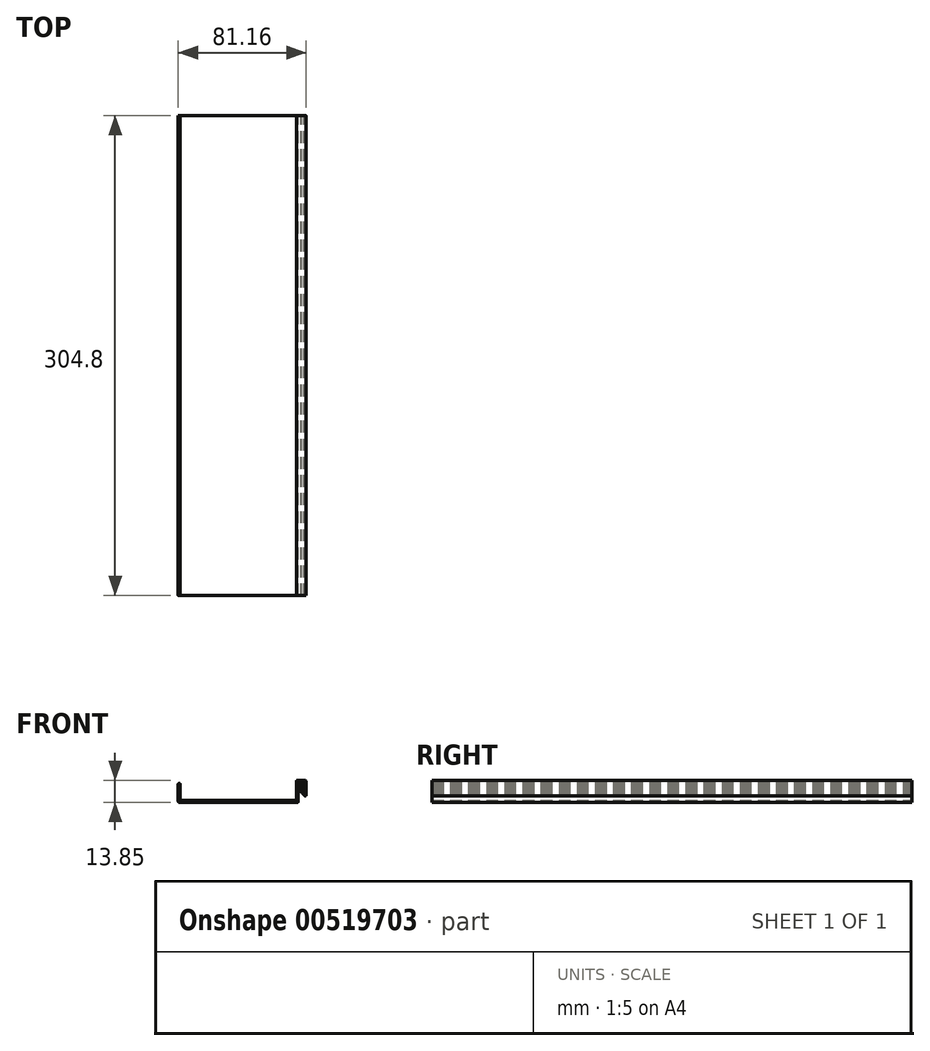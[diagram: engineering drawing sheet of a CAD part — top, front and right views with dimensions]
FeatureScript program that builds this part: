
annotation { "Feature Type Name" : "Feature", "Feature Type Description" : "" }
export const myFeature = defineFeature(function(context is Context, id is Id, definition is map)
    precondition{}
    {
        {
            var Q0;
            Q0=qCreatedBy(makeId("Front.planeOp"),FACE);
            var sketch = newSketch(context, id + "F0", { "sketchPlane" : qUnion([Q0])});
            skArc(sketch, "E0", {"start": v(-471.73, -378.6) * mm, "mid": v(-471.73, -378.44) * mm, "end": v(-471.88, -378.35) * mm});
            skArc(sketch, "E1", {"start": v(-475.36, -380.7) * mm, "mid": v(-473.26, -380.15) * mm, "end": v(-471.73, -378.6) * mm});
            skArc(sketch, "E2", {"start": v(-475.5, -380.45) * mm, "mid": v(-475.5, -380.61) * mm, "end": v(-475.36, -380.7) * mm});
            skArc(sketch, "E3", {"start": v(-471.88, -378.35) * mm, "mid": v(-473.98, -378.9) * mm, "end": v(-475.5, -380.45) * mm});
            skArc(sketch, "E4", {"start": v(-471.73, -372.86) * mm, "mid": v(-471.73, -372.7) * mm, "end": v(-471.88, -372.6) * mm});
            skArc(sketch, "E5", {"start": v(-475.36, -374.95) * mm, "mid": v(-473.26, -374.4) * mm, "end": v(-471.73, -372.86) * mm});
            skArc(sketch, "E6", {"start": v(-475.5, -374.7) * mm, "mid": v(-475.5, -374.87) * mm, "end": v(-475.36, -374.95) * mm});
            skArc(sketch, "E7", {"start": v(-471.88, -372.6) * mm, "mid": v(-473.98, -373.15) * mm, "end": v(-475.5, -374.7) * mm});
            skArc(sketch, "E8", {"start": v(-467.73, -383.43) * mm, "mid": v(-467.59, -383.35) * mm, "end": v(-467.59, -383.18) * mm});
            skArc(sketch, "E9", {"start": v(-471.36, -381.34) * mm, "mid": v(-469.83, -382.89) * mm, "end": v(-467.73, -383.43) * mm});
            skArc(sketch, "E10", {"start": v(-471.21, -381.09) * mm, "mid": v(-471.36, -381.17) * mm, "end": v(-471.36, -381.34) * mm});
            skArc(sketch, "E11", {"start": v(-467.59, -383.18) * mm, "mid": v(-469.1, -381.63) * mm, "end": v(-471.21, -381.09) * mm});
            skArc(sketch, "E12", {"start": v(-467.73, -377.9) * mm, "mid": v(-467.59, -377.82) * mm, "end": v(-467.59, -377.65) * mm});
            skArc(sketch, "E13", {"start": v(-471.36, -375.8) * mm, "mid": v(-469.83, -377.36) * mm, "end": v(-467.73, -377.9) * mm});
            skArc(sketch, "E14", {"start": v(-471.21, -375.56) * mm, "mid": v(-471.36, -375.64) * mm, "end": v(-471.36, -375.8) * mm});
            skArc(sketch, "E15", {"start": v(-467.59, -377.65) * mm, "mid": v(-469.1, -376.1) * mm, "end": v(-471.21, -375.56) * mm});
            skArc(sketch, "E16", {"start": v(-626.74, -370.02) * mm, "mid": v(-627.46, -370.32) * mm, "end": v(-627.75, -371.04) * mm});
            skLineSegment(sketch, "E17", {"start": v(-626.48, -370.02) * mm, "end": v(-626.74, -370.02) * mm});
            skArc(sketch, "E18", {"start": v(-625.47, -371.04) * mm, "mid": v(-625.77, -370.32) * mm, "end": v(-626.48, -370.02) * mm});
            skLineSegment(sketch, "E19", {"start": v(-625.47, -390.85) * mm, "end": v(-625.47, -371.04) * mm});
            skArc(sketch, "E20", {"start": v(-478.66, -391.87) * mm, "mid": v(-477.94, -391.57) * mm, "end": v(-477.64, -390.85) * mm});
            skArc(sketch, "E21", {"start": v(-476.62, -366.47) * mm, "mid": v(-477.34, -366.77) * mm, "end": v(-477.64, -367.48) * mm});
            skArc(sketch, "E22", {"start": v(-466.46, -386.28) * mm, "mid": v(-465.75, -385.98) * mm, "end": v(-465.45, -385.26) * mm});
            skArc(sketch, "E23", {"start": v(-467.73, -385.26) * mm, "mid": v(-467.44, -385.98) * mm, "end": v(-466.72, -386.28) * mm});
            skArc(sketch, "E24", {"start": v(-474.34, -368.75) * mm, "mid": v(-475.06, -369.05) * mm, "end": v(-475.35, -369.77) * mm});
            skArc(sketch, "E25", {"start": v(-476.37, -394.15) * mm, "mid": v(-475.65, -393.86) * mm, "end": v(-475.35, -393.14) * mm});
            skArc(sketch, "E26", {"start": v(-467.73, -369.77) * mm, "mid": v(-468.03, -369.05) * mm, "end": v(-468.75, -368.75) * mm});
            skArc(sketch, "E27", {"start": v(-627.75, -393.14) * mm, "mid": v(-627.46, -393.86) * mm, "end": v(-626.74, -394.15) * mm});
            skLineSegment(sketch, "E28", {"start": v(-477.64, -390.85) * mm, "end": v(-477.64, -367.48) * mm});
            skLineSegment(sketch, "E29", {"start": v(-624.45, -391.87) * mm, "end": v(-478.66, -391.87) * mm});
            skLineSegment(sketch, "E30", {"start": v(-476.62, -366.47) * mm, "end": v(-466.46, -366.47) * mm});
            skLineSegment(sketch, "E31", {"start": v(-475.35, -393.14) * mm, "end": v(-475.35, -369.77) * mm});
            skLineSegment(sketch, "E32", {"start": v(-474.34, -368.75) * mm, "end": v(-468.75, -368.75) * mm});
            skLineSegment(sketch, "E33", {"start": v(-467.73, -369.77) * mm, "end": v(-467.73, -385.26) * mm});
            skLineSegment(sketch, "E34", {"start": v(-466.72, -386.28) * mm, "end": v(-466.46, -386.28) * mm});
            skLineSegment(sketch, "E35", {"start": v(-465.45, -367.48) * mm, "end": v(-465.45, -385.26) * mm});
            skArc(sketch, "E36", {"start": v(-465.45, -367.48) * mm, "mid": v(-465.75, -366.77) * mm, "end": v(-466.46, -366.47) * mm});
            skArc(sketch, "E37", {"start": v(-625.47, -390.85) * mm, "mid": v(-625.17, -391.57) * mm, "end": v(-624.45, -391.87) * mm});
            skLineSegment(sketch, "E38", {"start": v(-627.75, -393.14) * mm, "end": v(-627.75, -371.04) * mm});
            skLineSegment(sketch, "E39", {"start": v(-626.74, -394.15) * mm, "end": v(-476.37, -394.15) * mm});
            skLineSegment(sketch, "E40", {"start": v(-625.22, -452.68) * mm, "end": v(-625.22, -457.12) * mm});
            skLineSegment(sketch, "E41", {"start": v(-472.82, -452.68) * mm, "end": v(-472.82, -457.12) * mm});
            skLineSegment(sketch, "E42", {"start": v(-625.22, -457.38) * mm, "end": v(-625.22, -457.12) * mm});
            skLineSegment(sketch, "E43", {"start": v(-472.82, -457.12) * mm, "end": v(-472.82, -457.38) * mm});
            skLineSegment(sketch, "E44", {"start": v(-625.22, -452.68) * mm, "end": v(-625.22, -452.42) * mm});
            skLineSegment(sketch, "E45", {"start": v(-472.82, -452.42) * mm, "end": v(-472.82, -452.68) * mm});
            skLineSegment(sketch, "E46", {"start": v(-625.22, -459.1) * mm, "end": v(-625.22, -457.38) * mm});
            skLineSegment(sketch, "E47", {"start": v(-472.82, -459.1) * mm, "end": v(-472.82, -457.38) * mm});
            skLineSegment(sketch, "E48", {"start": v(-625.22, -459.34) * mm, "end": v(-625.22, -459.1) * mm});
            skLineSegment(sketch, "E49", {"start": v(-472.82, -459.1) * mm, "end": v(-472.82, -459.34) * mm});
            skSolve(sketch);
        }
        {
            var Q0;
            {var subQ13=sQuery(id+"F0.wireOp",EDGE,"E2");Q0=makeQuery(id+"F0.imprint","IMPRINT",FACE,{"disambiguationData":[TD([[makeQuery(id+"F0.imprint","IMPRINT",EDGE,{"derivedFrom":subQ13}),-1.0]])]});}
            var Q1;
            {var subQ0=sQuery(id+"F0.wireOp",EDGE,"E4");Q1=makeQuery(id+"F0.imprint","IMPRINT",FACE,{"disambiguationData":[TD([[makeQuery(id+"F0.imprint","IMPRINT",EDGE,{"derivedFrom":subQ0}),1.0]])]});}
            var Q2;
            {var subQ0=sQuery(id+"F0.wireOp",EDGE,"E14");Q2=makeQuery(id+"F0.imprint","IMPRINT",FACE,{"disambiguationData":[TD([[makeQuery(id+"F0.imprint","IMPRINT",EDGE,{"derivedFrom":subQ0}),1.0]])]});}
            var Q3;
            {var subQ0=sQuery(id+"F0.wireOp",EDGE,"E0");Q3=makeQuery(id+"F0.imprint","IMPRINT",FACE,{"disambiguationData":[TD([[makeQuery(id+"F0.imprint","IMPRINT",EDGE,{"derivedFrom":subQ0}),1.0]])]});}
            var Q4;
            {var subQ3=sQuery(id+"F0.wireOp",EDGE,"E10");Q4=makeQuery(id+"F0.imprint","IMPRINT",FACE,{"disambiguationData":[TD([[makeQuery(id+"F0.imprint","IMPRINT",EDGE,{"derivedFrom":subQ3}),1.0]])]});}
            extrude(context, id + "F1", {"entities" : qUnion([Q0, Q1, Q2, Q3, Q4]), "depth" : 609.6 * mm, "offsetDistance" : 25.4 * mm});
        }
        {
            var Q0;
            Q0=makeQuery(id+"F1.opExtrude","SWEPT_BODY",BODY,{"disambiguationData":[OSD([sQuery(id+"F0.wireOp",EDGE,"E0"),sQuery(id+"F0.wireOp",EDGE,"E1"),sQuery(id+"F0.wireOp",EDGE,"E3"),sQuery(id+"F0.wireOp",EDGE,"E31")])]});
            var Q1;
            Q1=makeQuery(id+"F1.opExtrude","SWEPT_BODY",BODY,{"disambiguationData":[OSD([sQuery(id+"F0.wireOp",EDGE,"E1"),sQuery(id+"F0.wireOp",EDGE,"E2"),sQuery(id+"F0.wireOp",EDGE,"E3"),sQuery(id+"F0.wireOp",EDGE,"E5"),sQuery(id+"F0.wireOp",EDGE,"E6"),sQuery(id+"F0.wireOp",EDGE,"E7"),sQuery(id+"F0.wireOp",EDGE,"E8"),sQuery(id+"F0.wireOp",EDGE,"E9"),sQuery(id+"F0.wireOp",EDGE,"E11"),sQuery(id+"F0.wireOp",EDGE,"E12"),sQuery(id+"F0.wireOp",EDGE,"E13"),sQuery(id+"F0.wireOp",EDGE,"E15"),sQuery(id+"F0.wireOp",EDGE,"E16"),sQuery(id+"F0.wireOp",EDGE,"E17"),sQuery(id+"F0.wireOp",EDGE,"E18"),sQuery(id+"F0.wireOp",EDGE,"E19"),sQuery(id+"F0.wireOp",EDGE,"E20"),sQuery(id+"F0.wireOp",EDGE,"E21"),sQuery(id+"F0.wireOp",EDGE,"E22"),sQuery(id+"F0.wireOp",EDGE,"E23"),sQuery(id+"F0.wireOp",EDGE,"E24"),sQuery(id+"F0.wireOp",EDGE,"E25"),sQuery(id+"F0.wireOp",EDGE,"E26"),sQuery(id+"F0.wireOp",EDGE,"E27"),sQuery(id+"F0.wireOp",EDGE,"E28"),sQuery(id+"F0.wireOp",EDGE,"E29"),sQuery(id+"F0.wireOp",EDGE,"E30"),sQuery(id+"F0.wireOp",EDGE,"E31"),sQuery(id+"F0.wireOp",EDGE,"E32"),sQuery(id+"F0.wireOp",EDGE,"E33"),sQuery(id+"F0.wireOp",EDGE,"E34"),sQuery(id+"F0.wireOp",EDGE,"E35"),sQuery(id+"F0.wireOp",EDGE,"E36"),sQuery(id+"F0.wireOp",EDGE,"E37"),sQuery(id+"F0.wireOp",EDGE,"E38"),sQuery(id+"F0.wireOp",EDGE,"E39")])]});
            var Q2;
            Q2=makeQuery(id+"F1.opExtrude","SWEPT_BODY",BODY,{"disambiguationData":[OSD([sQuery(id+"F0.wireOp",EDGE,"E4"),sQuery(id+"F0.wireOp",EDGE,"E5"),sQuery(id+"F0.wireOp",EDGE,"E7"),sQuery(id+"F0.wireOp",EDGE,"E31")])]});
            var Q3;
            Q3=makeQuery(id+"F1.opExtrude","SWEPT_BODY",BODY,{"disambiguationData":[OSD([sQuery(id+"F0.wireOp",EDGE,"E9"),sQuery(id+"F0.wireOp",EDGE,"E10"),sQuery(id+"F0.wireOp",EDGE,"E11"),sQuery(id+"F0.wireOp",EDGE,"E33")])]});
            var Q4;
            Q4=makeQuery(id+"F1.opExtrude","SWEPT_BODY",BODY,{"disambiguationData":[OSD([sQuery(id+"F0.wireOp",EDGE,"E13"),sQuery(id+"F0.wireOp",EDGE,"E14"),sQuery(id+"F0.wireOp",EDGE,"E15"),sQuery(id+"F0.wireOp",EDGE,"E33")])]});
            var Q5;
            Q5=qCreatedBy(makeId("Origin.pointOp"),VERTEX);
            transform(context, id + "F2", {"entities" : qUnion([Q0, Q1, Q2, Q3, Q4]), "transformType" : TransformType.SCALE_UNIFORMLY, "scale" : .5, "scalePoint" : qUnion([Q5]), "makeCopy" : false});
        }
    });
